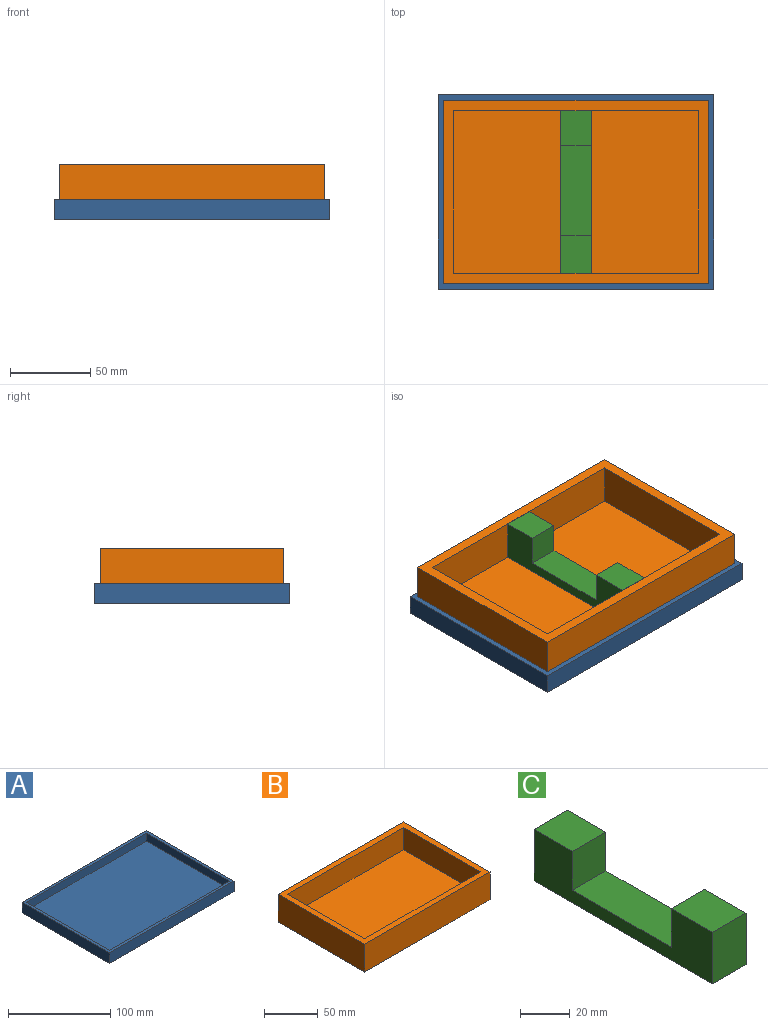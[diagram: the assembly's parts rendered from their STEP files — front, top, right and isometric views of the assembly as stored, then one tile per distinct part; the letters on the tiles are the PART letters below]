
ASSEMBLY  parts=3 mates=2
PART A: 11 faces, bbox 172x121.2x12.7 mm
  f0: plane 165.61x9.53mm, normal (0,-1,0), area 1577.4mm2, adj f1,f7,f8,f10
  f1: plane 114.81x9.53mm, normal (-1,0,0), area 1093.5mm2, adj f0,f2,f8,f10
  f2: plane 165.61x9.53mm, normal (0,1,0), area 1577.4mm2, adj f1,f7,f8,f10
  f3: plane 171.96x12.7mm, normal (0,-1,0), area 2183.9mm2, adj f4,f6,f8,f9
  f4: plane 121.16x12.7mm, normal (1,0,0), area 1538.7mm2, adj f3,f5,f8,f9
  f5: plane 171.96x12.7mm, normal (0,1,0), area 2183.9mm2, adj f4,f6,f8,f9
  f6: plane 121.16x12.7mm, normal (-1,0,0), area 1538.7mm2, adj f3,f5,f8,f9
  f7: plane 114.81x9.53mm, normal (1,0,0), area 1093.5mm2, adj f0,f2,f8,f10
  f8: plane 171.96x121.16mm, normal (0,0,1), area 1821mm2, adj f0,f1,f2,f3,f4,f5,f6,f7
  f9: plane 171.96x121.16mm, normal (0,0,-1), area 20834.1mm2, adj f3,f4,f5,f6
  f10: plane 165.61x114.81mm, normal (0,0,1), area 19013.1mm2, adj f0,f1,f2,f7
PART B: 11 faces, bbox 165.1x114.3x31.8 mm
  f0: plane 165.1x114.3mm, normal (0,0,1), area 3387.1mm2, adj f1,f2,f3,f4,f6,f7,f8,f9
  f1: plane 114.3x31.75mm, normal (1,0,0), area 3629mm2, adj f0,f2,f4,f5
  f2: plane 165.1x31.75mm, normal (0,1,0), area 5241.9mm2, adj f0,f1,f3,f5
  f3: plane 114.3x31.75mm, normal (-1,0,0), area 3629mm2, adj f0,f2,f4,f5
  f4: plane 165.1x31.75mm, normal (0,-1,0), area 5241.9mm2, adj f0,f1,f3,f5
  f5: plane 165.1x114.3mm, normal (0,0,-1), area 18870.9mm2, adj f1,f2,f3,f4
  f6: plane 101.6x25.4mm, normal (-1,0,0), area 2580.6mm2, adj f0,f7,f9,f10
  f7: plane 152.4x25.4mm, normal (0,-1,0), area 3871mm2, adj f0,f6,f8,f10
  f8: plane 101.6x25.4mm, normal (1,0,0), area 2580.6mm2, adj f0,f7,f9,f10
  f9: plane 152.4x25.4mm, normal (0,1,0), area 3871mm2, adj f0,f6,f8,f10
  f10: plane 152.4x101.6mm, normal (0,0,1), area 15483.8mm2, adj f6,f7,f8,f9
PART C: 10 faces, bbox 19.1x101.6x25.4 mm
  f0: plane 23.47x19.05mm, normal (0,0,1), area 447.1mm2, adj f1,f5,f6,f7
  f1: plane 101.6x25.4mm, normal (1,0,0), area 1508.4mm2, adj f0,f2,f3,f4,f5,f7,f8,f9
  f2: plane 101.6x19.05mm, normal (0,0,-1), area 1935.5mm2, adj f1,f3,f5,f6
  f3: plane 25.4x19.05mm, normal (0,1,0), area 483.9mm2, adj f1,f2,f4,f6
  f4: plane 21.85x19.05mm, normal (0,0,1), area 416.2mm2, adj f1,f3,f6,f8
  f5: plane 25.4x19.05mm, normal (0,-1,0), area 483.9mm2, adj f0,f1,f2,f6
  f6: plane 101.6x25.4mm, normal (-1,0,0), area 1508.4mm2, adj f0,f2,f3,f4,f5,f7,f8,f9
  f7: plane 19.05x19.05mm, normal (0,1,0), area 362.9mm2, adj f0,f1,f6,f9
  f8: plane 19.05x19.05mm, normal (0,-1,0), area 362.9mm2, adj f1,f4,f6,f9
  f9: plane 56.29x19.05mm, normal (0,0,1), area 1072.2mm2, adj f1,f6,f7,f8
PLACE A t=(-55.53,-72.82,-41.47)mm
PLACE B t=(-55.53,-72.82,-38.29)mm
PLACE C t=(-65.05,131.46,-82.56)mm
MATE fastened C.f2 <-> B.f10  axis (0,0,-1) through (-55.53,-72.82,-31.94)mm
MATE fastened A.f10 <-> B.f5  axis (0,0,1) through (-55.53,-72.82,-38.29)mm
